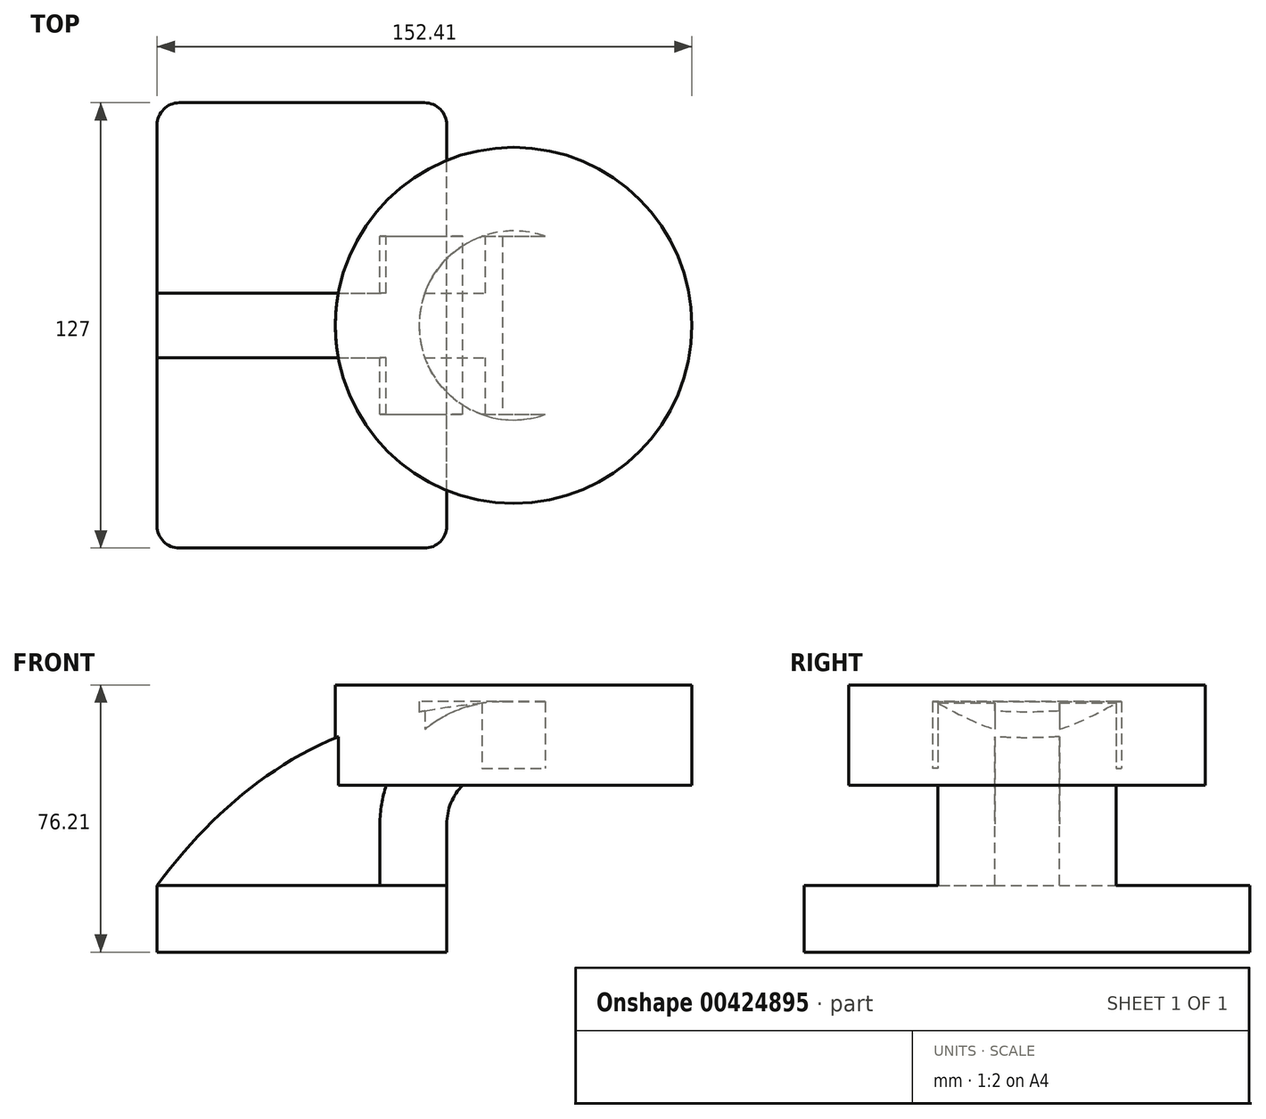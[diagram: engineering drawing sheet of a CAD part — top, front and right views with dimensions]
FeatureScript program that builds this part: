
annotation { "Feature Type Name" : "Feature", "Feature Type Description" : "" }
export const myFeature = defineFeature(function(context is Context, id is Id, definition is map)
    precondition{}
    {
        {
            var Q0;
            Q0=qCreatedBy(makeId("Front.planeOp"),FACE);
            var sketch = newSketch(context, id + "F0", { "sketchPlane" : qUnion([Q0])});
            skLineSegment(sketch, "E0.bottom", {"start": v(-41.28, -9.53) * mm, "end": v(41.28, -9.53) * mm});
            skLineSegment(sketch, "E0.top", {"start": v(-41.28, 9.52) * mm, "end": v(41.28, 9.52) * mm});
            skLineSegment(sketch, "E0.left", {"start": v(-41.28, -9.53) * mm, "end": v(-41.28, 9.52) * mm});
            skLineSegment(sketch, "E0.right", {"start": v(41.28, -9.53) * mm, "end": v(41.28, 9.52) * mm});
            skPoint(sketch, "E0.middle", {"position": v(0, 0) * mm});
            skLineSegment(sketch, "E1.bottom", {"start": v(60.32, 38.1) * mm, "end": v(111.12, 38.1) * mm});
            skLineSegment(sketch, "E1.top", {"start": v(60.32, 66.68) * mm, "end": v(111.12, 66.68) * mm});
            skLineSegment(sketch, "E1.left", {"start": v(60.32, 38.1) * mm, "end": v(60.32, 66.68) * mm});
            skLineSegment(sketch, "E1.right", {"start": v(111.12, 38.1) * mm, "end": v(111.12, 66.68) * mm});
            skPoint(sketch, "E1.middle", {"position": v(85.72, 52.39) * mm});
            skLineSegment(sketch, "E2", {"start": v(41.28, 9.52) * mm, "end": v(41.28, 27) * mm});
            skArc(sketch, "E3", {"start": v(41.27, 27) * mm, "mid": v(45.92, 38.23) * mm, "end": v(57.15, 42.88) * mm});
            skLineSegment(sketch, "E4", {"start": v(57.15, 42.88) * mm, "end": v(87.27, 42.88) * mm});
            skLineSegment(sketch, "E5.0", {"start": v(57.15, 61.93) * mm, "end": v(87.27, 61.93) * mm});
            skArc(sketch, "E5.1", {"start": v(22.22, 27) * mm, "mid": v(32.45, 51.7) * mm, "end": v(57.15, 61.93) * mm});
            skLineSegment(sketch, "E5.2", {"start": v(22.22, 9.52) * mm, "end": v(22.22, 27) * mm});
            skLineSegment(sketch, "E6", {"start": v(87.27, 42.88) * mm, "end": v(87.27, 61.93) * mm});
            skFitSpline(sketch, "E7", {"points": [v(-41.28, 9.52) * mm, v(57.15, 61.93) * mm], "startDerivative": vector(70.17, 93.25) * mm, "endDerivative": vector(141.8, 8.2) * mm});
            skSolve(sketch);
        }
        {
            var Q0;
            Q0=makeQuery(id+"F0.imprint","IMPRINT",FACE,{"disambiguationData":[TD([[makeQuery(id+"F0.imprint","IMPRINT",EDGE,{"derivedFrom":sQuery(id+"F0.wireOp",EDGE,"E0.bottom")}),1.0]])]});
            extrude(context, id + "F1", {"entities" : qUnion([Q0]), "endBound" : BoundingType.SYMMETRIC, "depth" : 127 * mm});
        }
        {
            var Q0;
            {var subQ0=sQuery(id+"F0.wireOp",EDGE,"E2");Q0=makeQuery(id+"F0.imprint","IMPRINT",FACE,{"disambiguationData":[TD([[makeQuery(id+"F0.imprint","IMPRINT",EDGE,{"derivedFrom":subQ0}),1.0]])]});}
            var Q1;
            {var subQ5=sQuery(id+"F0.wireOp",EDGE,"E6");Q1=makeQuery(id+"F0.imprint","IMPRINT",FACE,{"disambiguationData":[TD([[makeQuery(id+"F0.imprint","IMPRINT",EDGE,{"derivedFrom":subQ5}),1.0]])]});}
            extrude(context, id + "F2", {"entities" : qUnion([Q0, Q1]), "operationType" : NewBodyOperationType.ADD, "endBound" : BoundingType.SYMMETRIC, "depth" : 50.8 * mm});
        }
        {
            var Q0;
            {var subQ3=sQuery(id+"F0.wireOp",EDGE,"E5.2");Q0=makeQuery(id+"F0.imprint","IMPRINT",FACE,{"disambiguationData":[TD([[makeQuery(id+"F0.imprint","IMPRINT",EDGE,{"derivedFrom":subQ3}),1.0]])]});}
            extrude(context, id + "F3", {"entities" : qUnion([Q0]), "operationType" : NewBodyOperationType.ADD, "endBound" : BoundingType.SYMMETRIC, "depth" : 18.41 * mm});
        }
        {
            var Q0;
            Q0=makeQuery(id+"F1.opExtrude","CAP_EDGE",EDGE,{"disambiguationData":[OSD([sQuery(id+"F0.wireOp",EDGE,"E0.left")])],"isStart":false});
            var Q1;
            Q1=makeQuery(id+"F1.opExtrude","CAP_EDGE",EDGE,{"disambiguationData":[OSD([sQuery(id+"F0.wireOp",EDGE,"E0.right")])],"isStart":false});
            var Q2;
            Q2=makeQuery(id+"F1.opExtrude","CAP_EDGE",EDGE,{"disambiguationData":[OSD([sQuery(id+"F0.wireOp",EDGE,"E0.right")])],"isStart":true});
            var Q3;
            Q3=makeQuery(id+"F1.opExtrude","CAP_EDGE",EDGE,{"disambiguationData":[OSD([sQuery(id+"F0.wireOp",EDGE,"E0.left")])],"isStart":true});
            fillet(context, id + "F4", {"entities" : qUnion([Q0, Q1, Q2, Q3]), "radius" : 6.35 * mm, "tangentPropagation" : true, "allowEdgeOverflow" : false});
        }
        {
            var Q0;
            {var subQ5=sQuery(id+"F0.wireOp",EDGE,"E1.bottom");Q0=makeQuery(id+"F0.imprint","IMPRINT",FACE,{"disambiguationData":[TD([[makeQuery(id+"F0.imprint","IMPRINT",EDGE,{"derivedFrom":subQ5}),1.0]])]});}
            var Q1;
            Q1=sQuery(id+"F0.wireOp",EDGE,"E1.left");
            revolve(context, id + "F5", {"operationType" : NewBodyOperationType.ADD, "entities" : qUnion([Q0]), "axis" : qUnion([Q1]), "revolveType" : RevolveType.FULL});
        }
    });
